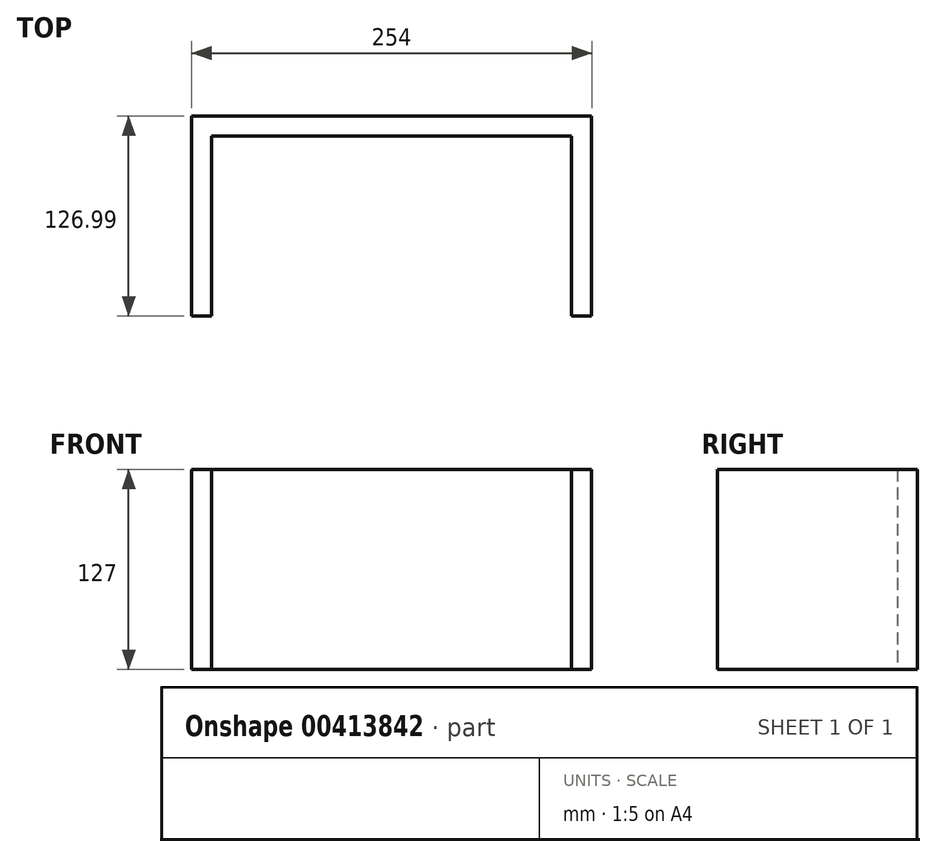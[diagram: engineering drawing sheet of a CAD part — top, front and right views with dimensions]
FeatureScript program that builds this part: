
annotation { "Feature Type Name" : "Feature", "Feature Type Description" : "" }
export const myFeature = defineFeature(function(context is Context, id is Id, definition is map)
    precondition{}
    {
        {
            var Q0;
            Q0=qCreatedBy(makeId("Top.planeOp"),FACE);
            var sketch = newSketch(context, id + "F0", { "sketchPlane" : qUnion([Q0])});
            skLineSegment(sketch, "E0.bottom", {"start": v(-149.78, 56.51) * mm, "end": v(104.22, 56.51) * mm});
            skLineSegment(sketch, "E0.top", {"start": v(-149.78, 43.81) * mm, "end": v(104.22, 43.81) * mm});
            skLineSegment(sketch, "E0.left", {"start": v(-149.78, 56.51) * mm, "end": v(-149.78, 43.81) * mm});
            skLineSegment(sketch, "E0.right", {"start": v(104.22, 56.51) * mm, "end": v(104.22, 43.81) * mm});
            skSolve(sketch);
        }
        {
            var Q0;
            Q0 = qSketchRegion(id + "F0", true);
            extrude(context, id + "F1", {"entities" : qUnion([Q0]), "depth" : 127 * mm});
        }
        {
            var Q0;
            Q0=qCreatedBy(makeId("Top.planeOp"),FACE);
            var sketch = newSketch(context, id + "F2", { "sketchPlane" : qUnion([Q0])});
            skLineSegment(sketch, "E1.bottom", {"start": v(-149.78, 43.82) * mm, "end": v(-137.08, 43.82) * mm});
            skLineSegment(sketch, "E1.top", {"start": v(-149.78, -70.48) * mm, "end": v(-137.08, -70.48) * mm});
            skLineSegment(sketch, "E1.left", {"start": v(-149.78, 43.82) * mm, "end": v(-149.78, -70.48) * mm});
            skLineSegment(sketch, "E1.right", {"start": v(-137.08, 43.82) * mm, "end": v(-137.08, -70.48) * mm});
            skSolve(sketch);
        }
        {
            var Q0;
            Q0=makeQuery(id+"F2.imprint","IMPRINT",FACE,{"disambiguationData":[TD([[makeQuery(id+"F2.imprint","IMPRINT",EDGE,{"derivedFrom":sQuery(id+"F2.wireOp",EDGE,"E1.bottom")}),-1.0]])]});
            extrude(context, id + "F3", {"entities" : qUnion([Q0]), "operationType" : NewBodyOperationType.ADD, "depth" : 127 * mm});
        }
        {
            var Q0;
            Q0=qCreatedBy(makeId("Top.planeOp"),FACE);
            var sketch = newSketch(context, id + "F4", { "sketchPlane" : qUnion([Q0])});
            skLineSegment(sketch, "E2.bottom", {"start": v(104.22, 43.82) * mm, "end": v(91.52, 43.82) * mm});
            skLineSegment(sketch, "E2.top", {"start": v(104.22, -70.48) * mm, "end": v(91.52, -70.48) * mm});
            skLineSegment(sketch, "E2.left", {"start": v(104.22, 43.82) * mm, "end": v(104.22, -70.48) * mm});
            skLineSegment(sketch, "E2.right", {"start": v(91.52, 43.82) * mm, "end": v(91.52, -70.48) * mm});
            skSolve(sketch);
        }
        {
            var Q0;
            Q0=makeQuery(id+"F4.imprint","IMPRINT",FACE,{"disambiguationData":[TD([[makeQuery(id+"F4.imprint","IMPRINT",EDGE,{"derivedFrom":sQuery(id+"F4.wireOp",EDGE,"E2.bottom")}),1.0]])]});
            extrude(context, id + "F5", {"entities" : qUnion([Q0]), "operationType" : NewBodyOperationType.ADD, "depth" : 127 * mm});
        }
    });
